# Revit family: BKEF-R-
name_source: partatom
category: Mechanical Equipment
units: mm (PartAtom-declared; Revit-internal decimal feet)

## family parameters
Always vertical = Yes
Cut with Voids When Loaded = No
OmniClass Number = 23.75.00.00
OmniClass Title = Climate Control (HVAC)
Part Type = Breaks Into
Room Calculation Point = No
Round Connector Dimension = Use Diameter
Shared = No
Work Plane-Based = No

## types (8) — shared parameters
D = 350 mm  [stored 1.14829 ft]
Description = Duct Fan
Frequency = 50 Hz
Insulation Class = F
Manufacturer = Bahçıvan Elektrik Motor San. ve Tic. Ltd. Şti.
Material = <By Category>
Model = BKEF-R
Protection Class = 55
R = 150 mm
URL = http://www.bahcivanmotor.com.tr

## per-type parameters (varying)
| type | A | Air Flow | B | C | Capacitor | Current | Power | RD | Sound Pressure Level dB(A) | Speed ( d/d ) | Voltage | Weight |
| BKEF-R 400M | 683 mm  [stored 2.24081 ft] | 4100.0 m³/h | 556 mm  [stored 1.82415 ft] | 603 mm | 15 | 3 A | 370 W | 228 mm | 45 | 1390 | 230 V | 52.00 kg |
| BKEF-R 450M | 683 mm  [stored 2.24081 ft] | 5400.0 m³/h | 572 mm | 603 mm | 20 | 5 A | 550 W | 228 mm | 48 | 1365 | 230 V | 65.00 kg |
| BKEF-R 500M | 683 mm  [stored 2.24081 ft] | 8200.0 m³/h | 623 mm  [stored 2.04396 ft] | 603 mm | 35 | 8 A | 1100 W | 228 mm | 52 | 1410 | 230 V | 77.00 kg |
| BKEF-R 560M | 813 mm  [stored 2.66732 ft] | 10800.0 m³/h | 690 mm  [stored 2.26378 ft] | 733 mm  [stored 2.40486 ft] | 50 | 14 A | 2200 W | 271 mm  [stored 0.889108 ft] | 55 | 1420 | 230 V | 95.00 kg |
| BKEF-R 400T | 683 mm  [stored 2.24081 ft] | 4100.0 m³/h | 556 mm  [stored 1.82415 ft] | 603 mm | 0 | 1 A | 370 W | 228 mm | 45 | 1390 | 380 V | 52.00 kg |
| BKEF-R 450T | 683 mm  [stored 2.24081 ft] | 5400.0 m³/h | 572 mm | 603 mm | 0 | 2 A | 550 W | 228 mm | 48 | 1365 | 380 V | 65.00 kg |
| BKEF-R 500T | 683 mm  [stored 2.24081 ft] | 8200.0 m³/h | 623 mm  [stored 2.04396 ft] | 603 mm | 0 | 3 A | 1100 W | 228 mm | 52 | 1410 | 380 V | 77.00 kg |
| BKEF-R 560T | 813 mm  [stored 2.66732 ft] | 10800.0 m³/h | 690 mm  [stored 2.26378 ft] | 733 mm  [stored 2.40486 ft] | 0 | 5 A | 2200 W | 271 mm  [stored 0.889108 ft] | 55 | 1420 | 380 V | 95.00 kg |

note: [stored X ft] marks values corroborated as IEEE doubles in the binary element streams (Revit-internal decimal feet)

## geometry (parser evidence)
native form markers: Sweep x2
no freeform markers — native parametric forms only
